# Revit family: BDG_BossDesign_Stng_MarnieWIP20
name_source: partatom
category: Furniture
revit_build: Autodesk Revit 2016 (Build: 20150220_1215(x64)
units: mm (PartAtom-declared; Revit-internal decimal feet)

## family parameters
Always vertical = Yes
Cut with Voids When Loaded = No
OmniClass Number = 23.40.20.00
OmniClass Title = General Furniture and Specialties
Room Calculation Point = No
Shared = Yes
Work Plane-Based = No

## types (8) — shared parameters
Assembly Code = E2020200
AssetType = Movable
BIMObjectName = BDG_BossDesign_Seating_Marnie
Category = Pr_40_50_12 : Chairs, seats and benches
DurationUnit = year
ExpectedLife = 5
IfcExportAs = IfcFurnishingElementType
IfcExportType = CHAIR
Keynote = Pr_40_50_12
ManufacturerName = Boss Design
ManufacturerURL = www.bossdesign.com
Material = Fabric/Leather
NBSDescription = Seating
NBSReference = 45-35-72/352
Name = Seating_Marnie_BossDesign
NominalLength = 710 mm
ProductInformation = www.bossdesign.com/product-list/marnie
SeatMaterial = BDG_Kvadrat_Fabric_Divina3_562
Shape = Rectangular
URL = www.bossdesign.com
Uniclass2015Code = Pr_40_50_12
Uniclass2015Title = Chairs, seats and benches
Uniclass2015Version = Products v1.10
Version = 1
WarrantyDurationLabor = 5
WarrantyDurationParts = 5
WarrantyDurationUnit = year

## per-type parameters (varying)
| type | FrameMaterial | Is4Legs | Is4LegsTimberFrame | IsHighBackSeating | IsMediumBackSeating | IsSledLegs | IsSwivelLegs | Model | ModelNumber | NominalHeight | NominalWidth | Size |
| High Back Fully Upholstered, 4 Star Base | BDG_Generic_Metal_Chrome | No | No | Yes | No | No | Yes | MRN/1 | MRN/1 | 1070 mm  [stored 3.5105 ft] | 790 mm  [stored 2.59186 ft] | 710 x 790 x 1070mm |
| Medium Back Fully Upholstered, 4 Star Base | BDG_Generic_Metal_Chrome | No | No | No | Yes | No | Yes | MRN/2 | MRN/2 | 810 mm | 780 mm  [stored 2.55906 ft] | 710 x 780 x 810mm |
| High Back Fully Upholstered, 4 Leg Powder Coated Base | BDG_Generic_Metal_White | Yes | No | Yes | No | No | No | MRN/3 | MRN/3 | 1070 mm  [stored 3.5105 ft] | 790 mm  [stored 2.59186 ft] | 710 x 790 x 1070mm |
| Medium Back Fully Upholstered, 4 Leg Powder Coated Base | BDG_Generic_Metal_White | Yes | No | No | Yes | No | No | MRN/4 | MRN/4 | 825 mm  [stored 2.70669 ft] | 780 mm  [stored 2.55906 ft] | 710 x 780 x 825mm |
| High Back Fully Upholstered, 4 Leg Oak Frame | BDG_Generic_Wood_Oak | No | Yes | Yes | No | No | No | MRN/3/OF | MRN/3/OF | 1070 mm  [stored 3.5105 ft] | 790 mm  [stored 2.59186 ft] | 710 x 790 x 1070mm |
| Medium Back Fully Upholstered, 4 Leg Oak Frame | BDG_Generic_Wood_Oak | No | Yes | No | Yes | No | No | MRN/4/OF | MRN/4/OF | 810 mm | 780 mm  [stored 2.55906 ft] | 710 x 780 x 810mm |
| High Back Fully Upholstered, Painted Sled Base | BDG_Generic_Metal_White | No | No | Yes | No | Yes | No | MRN/5 | MRN/5 | 1065 mm  [stored 3.49409 ft] | 790 mm  [stored 2.59186 ft] | 710 x 790 x 1065mm |
| Medium Back Fully Upholstered, Painted Sled Base | BDG_Generic_Metal_White | No | No | No | Yes | Yes | No | MRN/6 | MRN/6 | 805 mm  [stored 2.64108 ft] | 780 mm  [stored 2.55906 ft] | 710 x 780 x 805mm |

note: column(s) folded — value = type name in every type: Description, ModelReference

note: [stored X ft] marks values corroborated as IEEE doubles in the binary element streams (Revit-internal decimal feet)

## geometry (parser evidence)
native form markers: Sweep x13
no freeform markers — native parametric forms only
